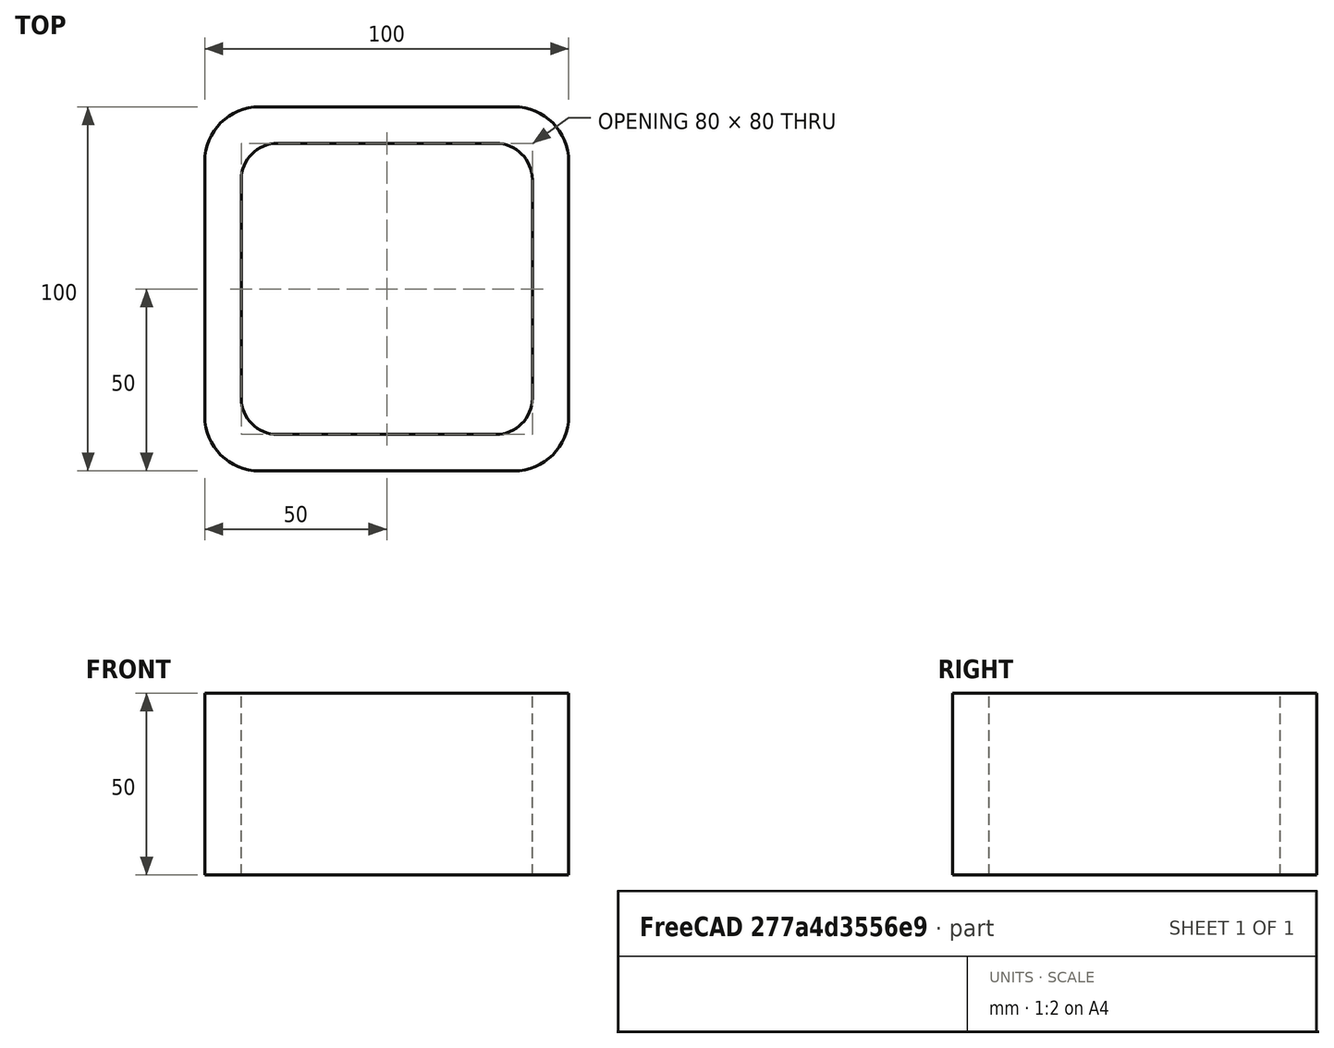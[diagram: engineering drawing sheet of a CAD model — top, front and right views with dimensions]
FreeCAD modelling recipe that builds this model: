
FCSTD DOCUMENT  (FreeCAD 0.15R4671 (Git))
Label: Square hollow section 100x100x10 EN10219 S235JRH
License: All rights reserved
LicenseURL: http://en.wikipedia.org/wiki/All_rights_reserved
objects: Sketcher::SketchObject×1, Part::Extrusion×1
note: 2 computed .brp shape members not serialized (recipe doc carries the construction recipe); baked Part::Feature solids carry a one-line shape summary decoded from their .brp

FEATURE [Sketcher::SketchObject] Sketch
  sketch-geometry (16):
    g0: LineSegment StartX=-30 StartY=40 StartZ=0 EndX=30 EndY=40 EndZ=0
    g1: LineSegment StartX=40 StartY=30 StartZ=0 EndX=40 EndY=-30 EndZ=0
    g2: LineSegment StartX=30 StartY=-40 StartZ=0 EndX=-30 EndY=-40 EndZ=0
    g3: LineSegment StartX=-40 StartY=-30 StartZ=0 EndX=-40 EndY=30 EndZ=0
    g4: LineSegment StartX=-35 StartY=50 StartZ=0 EndX=35 EndY=50 EndZ=0
    g5: LineSegment StartX=50 StartY=35 StartZ=0 EndX=50 EndY=-35 EndZ=0
    g6: LineSegment StartX=35 StartY=-50 StartZ=0 EndX=-35 EndY=-50 EndZ=0
    g7: LineSegment StartX=-50 StartY=-35 StartZ=0 EndX=-50 EndY=35 EndZ=0
    g8: ArcOfCircle CenterX=-30 CenterY=30 CenterZ=0 NormalX=0 NormalY=0 NormalZ=1 Radius=10 StartAngle=1.5708 EndAngle=3.14159
    g9: ArcOfCircle CenterX=30 CenterY=30 CenterZ=0 NormalX=0 NormalY=0 NormalZ=1 Radius=10 StartAngle=0 EndAngle=1.5708
    g10: ArcOfCircle CenterX=30 CenterY=-30 CenterZ=0 NormalX=0 NormalY=0 NormalZ=1 Radius=10 StartAngle=4.71239 EndAngle=6.28319
    g11: ArcOfCircle CenterX=-30 CenterY=-30 CenterZ=0 NormalX=0 NormalY=0 NormalZ=1 Radius=10 StartAngle=3.14159 EndAngle=4.71239
    g12: ArcOfCircle CenterX=35 CenterY=35 CenterZ=0 NormalX=0 NormalY=0 NormalZ=1 Radius=15 StartAngle=0 EndAngle=1.5708
    g13: ArcOfCircle CenterX=35 CenterY=-35 CenterZ=0 NormalX=0 NormalY=0 NormalZ=1 Radius=15 StartAngle=4.71239 EndAngle=6.28319
    g14: ArcOfCircle CenterX=-35 CenterY=-35 CenterZ=0 NormalX=0 NormalY=0 NormalZ=1 Radius=15 StartAngle=3.14159 EndAngle=4.71239
    g15: ArcOfCircle CenterX=-35 CenterY=35 CenterZ=0 NormalX=0 NormalY=0 NormalZ=1 Radius=15 StartAngle=1.5708 EndAngle=3.14159
  constraints (36):
    c: Horizontal(g2)
    c: Vertical(g3)
    c: Horizontal(g6)
    c: Vertical(g7)
    c: Tangent(g3,g8) = 1.5708
    c: Tangent(g0,g8) = 1.5708
    c: Tangent(g0,g9) = 1.5708
    c: Tangent(g1,g9) = 1.5708
    c: Tangent(g1,g10) = 1.5708
    c: Tangent(g2,g10) = 1.5708
    c: Tangent(g2,g11) = 1.5708
    c: Tangent(g3,g11) = 1.5708
    c: Tangent(g4,g12) = 1.5708
    c: Tangent(g5,g12) = 1.5708
    c: Tangent(g5,g13) = 1.5708
    c: Tangent(g6,g13) = 1.5708
    c: Tangent(g6,g14) = 1.5708
    c: Tangent(g7,g14) = 1.5708
    c: Tangent(g7,g15) = 1.5708
    c: Tangent(g4,g15) = 1.5708
    c: Equal(g9,g8)
    c: Equal(g9,g11)
    c: Equal(g9,g10)
    c: Equal(g12,g15)
    c: Equal(g12,g14)
    c: Equal(g12,g13)
    c: Symmetric(g4,g6,g-1)
    c: Symmetric(g7,g5,g-2)
    c: DistanceY(g4,g6) = -100
    c: DistanceX(g7,g5) = 100
    c: Symmetric(g3,g1,g-2)
    c: Symmetric(g0,g2,g-1)
    c: DistanceY(g0,g4) = 10
    c: DistanceX(g5,g1) = -10
    c: Radius(g9) = 10
    c: Radius(g12) = 15
FEATURE [Part::Extrusion] Extrude  label="Square hollow section 100x100x10 EN10219 S235JRH"
  Base = -> Sketch
  Dir = (0,0,50)
  Solid = true
